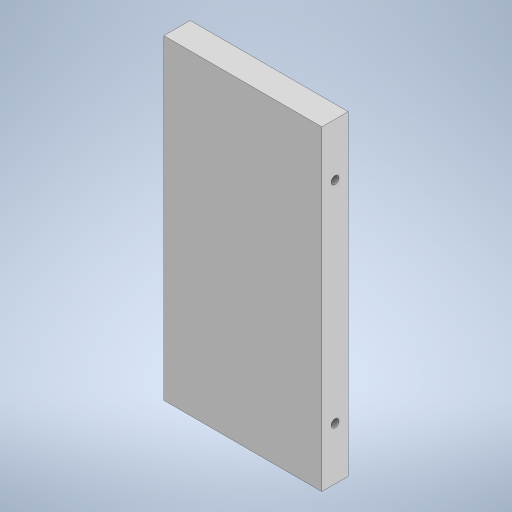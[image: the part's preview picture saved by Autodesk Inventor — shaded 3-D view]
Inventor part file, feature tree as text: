
AUTODESK INVENTOR PART (.ipt)
format: ipt  version: 2023 (Build 270158000, 158)  size: 221,696 bytes
history: native  units: mm
features: extrude x3, sketch x3
ambient origin geometry x8: Origin, YZ Plane, XZ Plane, XY Plane, X Axis, Y Axis, Z Axis, Center Point
bodies: Solide1 (feature_tree)
feature tree (6):
  extrude  "Extrusion1"  Depth=120.0mm
  sketch  "Esquisse2"
  extrude  "Extrusion2"  Depth=60.0mm
  extrude  "Extrusion3"  Depth=10.0mm TaperAngle=0.0deg
  sketch  "Esquisse1"
  sketch  "Esquisse3"
